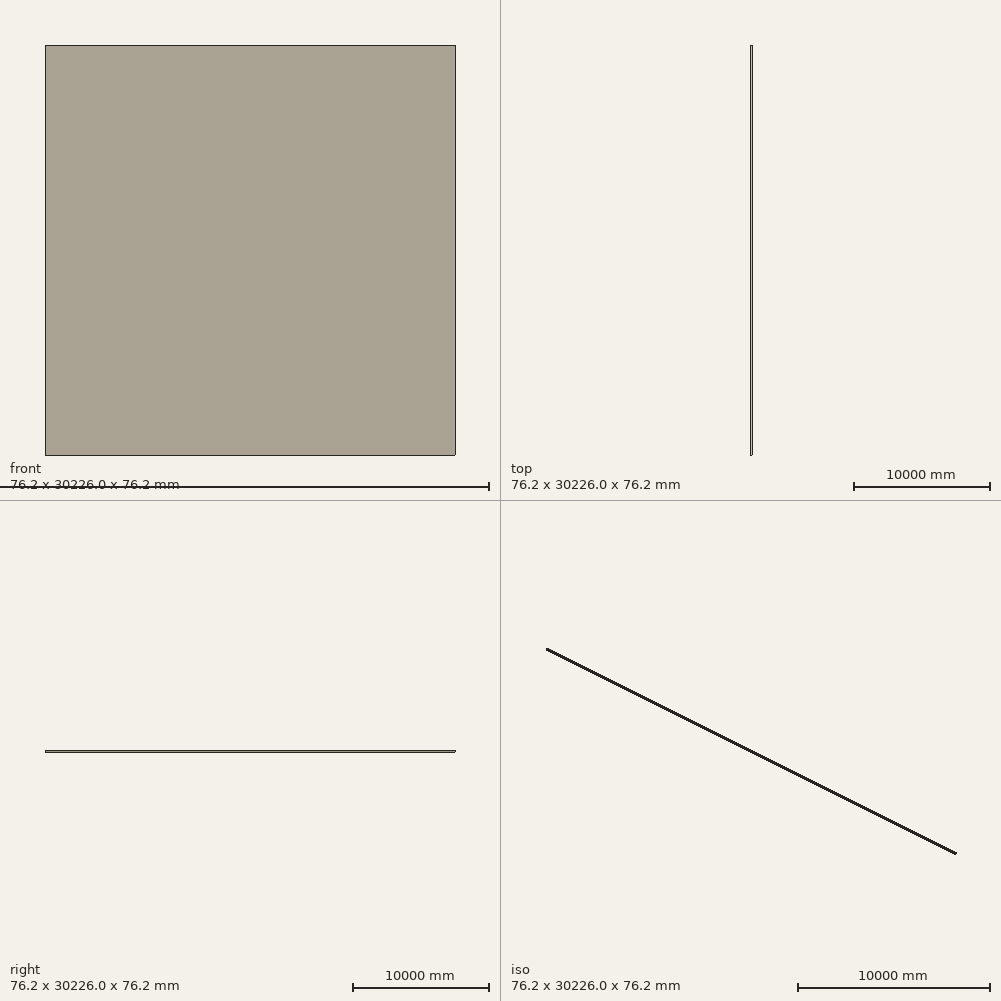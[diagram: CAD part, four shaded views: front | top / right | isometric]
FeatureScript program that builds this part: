
annotation { "Feature Type Name" : "Feature", "Feature Type Description" : "" }
export const myFeature = defineFeature(function(context is Context, id is Id, definition is map)
    precondition{}
    {
        {
            var Q0;
            Q0=qCreatedBy(makeId("Front.planeOp"),FACE);
            var sketch = newSketch(context, id + "F0", { "sketchPlane" : qUnion([Q0])});
            skLineSegment(sketch, "E0.bottom", {"start": v(0, 0) * mm, "end": v(76.2, 0) * mm});
            skLineSegment(sketch, "E0.top", {"start": v(0, 76.2) * mm, "end": v(76.2, 76.2) * mm});
            skLineSegment(sketch, "E0.left", {"start": v(0, 0) * mm, "end": v(0, 76.2) * mm});
            skLineSegment(sketch, "E0.right", {"start": v(76.2, 0) * mm, "end": v(76.2, 76.2) * mm});
            skSolve(sketch);
        }
        {
            var Q0;
            Q0=makeQuery(id+"F0.imprint","IMPRINT",FACE,{"disambiguationData":[TD([[makeQuery(id+"F0.imprint","IMPRINT",EDGE,{"derivedFrom":sQuery(id+"F0.wireOp",EDGE,"E0.bottom")}),1.0]])]});
            extrude(context, id + "F1", {"entities" : qUnion([Q0]), "depth" : 30226 * mm, "offsetDistance" : 25.4 * mm});
        }
    });
